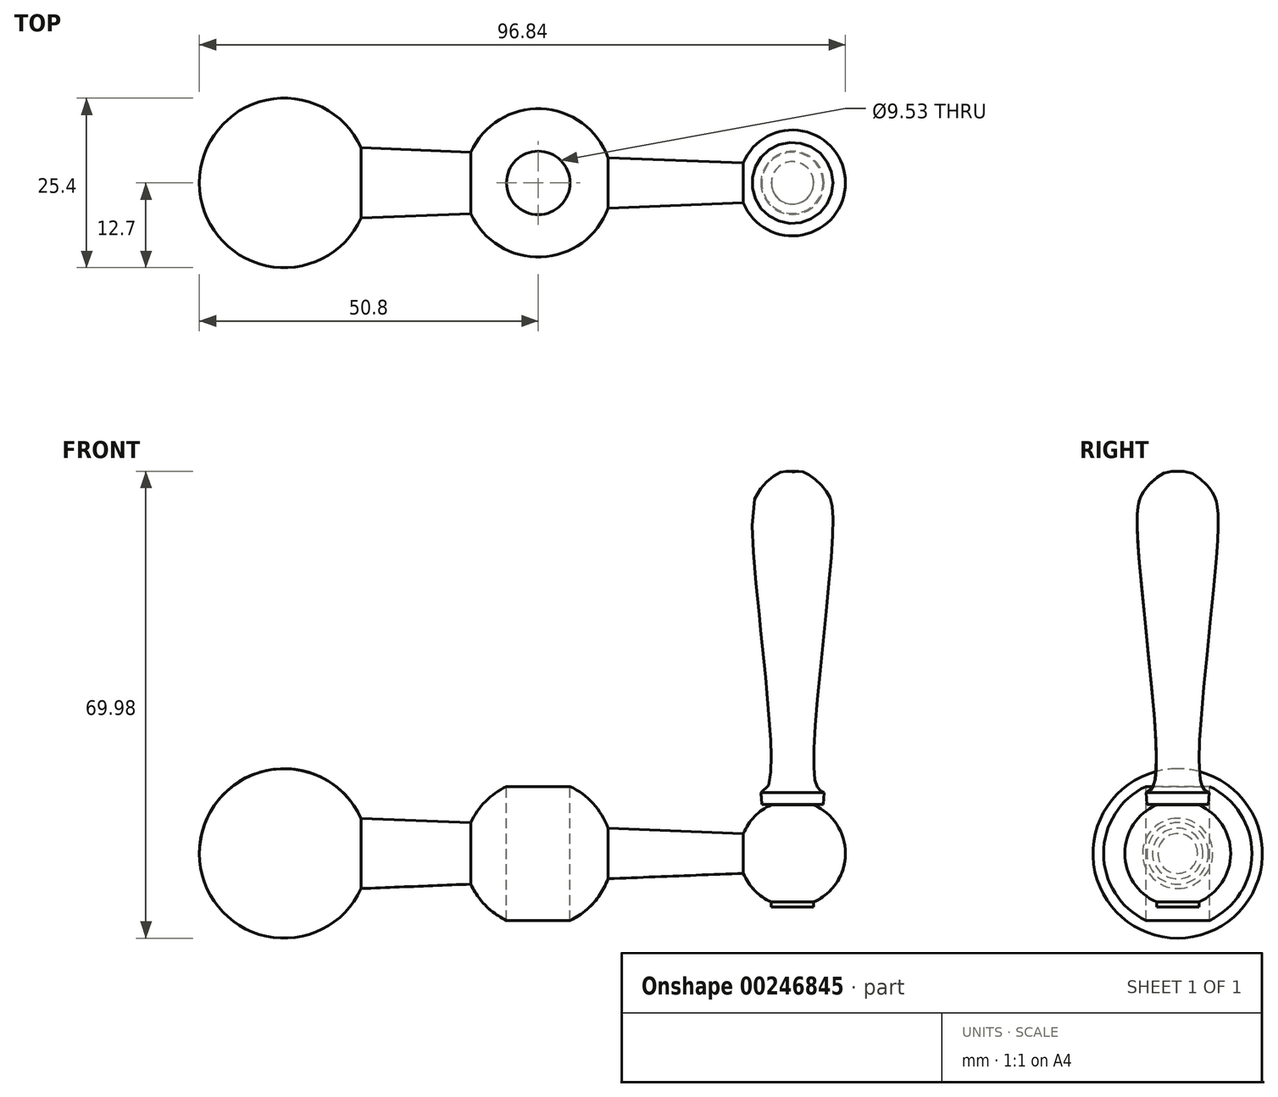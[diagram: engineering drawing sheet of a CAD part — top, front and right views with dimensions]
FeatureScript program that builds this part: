
annotation { "Feature Type Name" : "Feature", "Feature Type Description" : "" }
export const myFeature = defineFeature(function(context is Context, id is Id, definition is map)
    precondition{}
    {
        {
            var Q0;
            Q0=qCreatedBy(makeId("Top.planeOp"),FACE);
            var sketch = newSketch(context, id + "F0", { "sketchPlane" : qUnion([Q0])});
            skCircle(sketch, "E0", {"center": v(0, 0) * mm, "radius": 4.76 * mm});
            skCircle(sketch, "E1", {"center": v(38.1, 0) * mm, "radius": 3.18 * mm});
            skSolve(sketch);
        }
        {
            var Q0;
            Q0=qCreatedBy(makeId("Front.planeOp"),FACE);
            var sketch = newSketch(context, id + "F1", { "sketchPlane" : qUnion([Q0])});
            skLineSegment(sketch, "E2", {"start": v(0, 0) * mm, "end": v(46.04, 0) * mm});
            skLineSegment(sketch, "E3", {"start": v(38.1, 7.94) * mm, "end": v(38.1, 57.15) * mm});
            skLineSegment(sketch, "E4", {"start": v(0, 0) * mm, "end": v(-50.8, 0) * mm});
            skArc(sketch, "E5", {"start": v(-26.54, 5.26) * mm, "mid": v(-40.8, 12.41) * mm, "end": v(-50.8, 0) * mm});
            skArc(sketch, "E6", {"start": v(46.04, 0) * mm, "mid": v(39.62, 7.8) * mm, "end": v(30.74, 2.98) * mm});
            skLineSegment(sketch, "E7.0", {"start": v(-26.54, 5.26) * mm, "end": v(-10.11, 4.6) * mm});
            skLineSegment(sketch, "E8.0", {"start": v(10.45, 3.79) * mm, "end": v(30.74, 2.98) * mm});
            skArc(sketch, "E9", {"start": v(10.45, 3.79) * mm, "mid": v(0.44, 11.1) * mm, "end": v(-10.11, 4.6) * mm});
            skSolve(sketch);
        }
        {
            var Q0;
            {var subQ1=sQuery(id+"F1.wireOp",EDGE,"E2");Q0=makeQuery(id+"F1.imprint","IMPRINT",FACE,{"disambiguationData":[TD([[makeQuery(id+"F1.imprint","IMPRINT",EDGE,{"derivedFrom":subQ1}),1.0]])]});}
            var Q1;
            Q1=sQuery(id+"F1.wireOp",EDGE,"E4");
            revolve(context, id + "F2", {"entities" : qUnion([Q0]), "axis" : qUnion([Q1]), "revolveType" : RevolveType.FULL});
        }
        {
            var Q0;
            Q0 = qSketchRegion(id + "F0", true);
            extrude(context, id + "F3", {"entities" : qUnion([Q0]), "operationType" : NewBodyOperationType.REMOVE, "oppositeDirection" : true, "depth" : 25.4 * mm, "hasSecondDirection" : true, "secondDirectionOppositeDirection" : false, "secondDirectionDepth" : 25.4 * mm});
        }
        {
            var Q0;
            Q0=qCreatedBy(makeId("Front.planeOp"),FACE);
            var sketch = newSketch(context, id + "F4", { "sketchPlane" : qUnion([Q0])});
            skLineSegment(sketch, "E10", {"start": v(0, 0) * mm, "end": v(38.1, 0) * mm});
            skLineSegment(sketch, "E11", {"start": v(38.1, 0) * mm, "end": v(38.1, 57.15) * mm});
            skFitSpline(sketch, "E12", {"points": [v(38.1, 57.15) * mm, v(39.8, 57.15) * mm, v(42.77, 54.8) * mm, v(44.17, 49.5) * mm, v(41.37, 11.78) * mm, v(42.46, 9.28) * mm, v(43.23, 9.1) * mm], "startDerivative": vector(17.5, 3.61) * mm, "endDerivative": vector(12.73, 1.98) * mm});
            skLineSegment(sketch, "E13", {"start": v(38.1, 0) * mm, "end": v(38.1, -8.02) * mm});
            skLineSegment(sketch, "E14", {"start": v(38.1, -8.02) * mm, "end": v(41.27, -8.02) * mm});
            skLineSegment(sketch, "E15", {"start": v(41.27, -8.02) * mm, "end": v(41.27, 7.32) * mm});
            skLineSegment(sketch, "E16", {"start": v(41.27, 7.32) * mm, "end": v(42.69, 7.32) * mm});
            skLineSegment(sketch, "E17", {"start": v(42.69, 7.32) * mm, "end": v(42.82, 9.13) * mm});
            skPoint(sketch, "E18.orphan", {"position": v(43.23, 14.61) * mm});
            skSolve(sketch);
        }
        {
            var Q0;
            Q0=makeQuery(id+"F4.imprint","IMPRINT",FACE,{"disambiguationData":[TD([[makeQuery(id+"F4.imprint","IMPRINT",EDGE,{"derivedFrom":sQuery(id+"F4.wireOp",EDGE,"E11")}),-1.0]])]});
            var Q1;
            Q1=sQuery(id+"F4.wireOp",EDGE,"E11");
            revolve(context, id + "F5", {"operationType" : NewBodyOperationType.ADD, "entities" : qUnion([Q0]), "axis" : qUnion([Q1]), "revolveType" : RevolveType.FULL});
        }
    });
